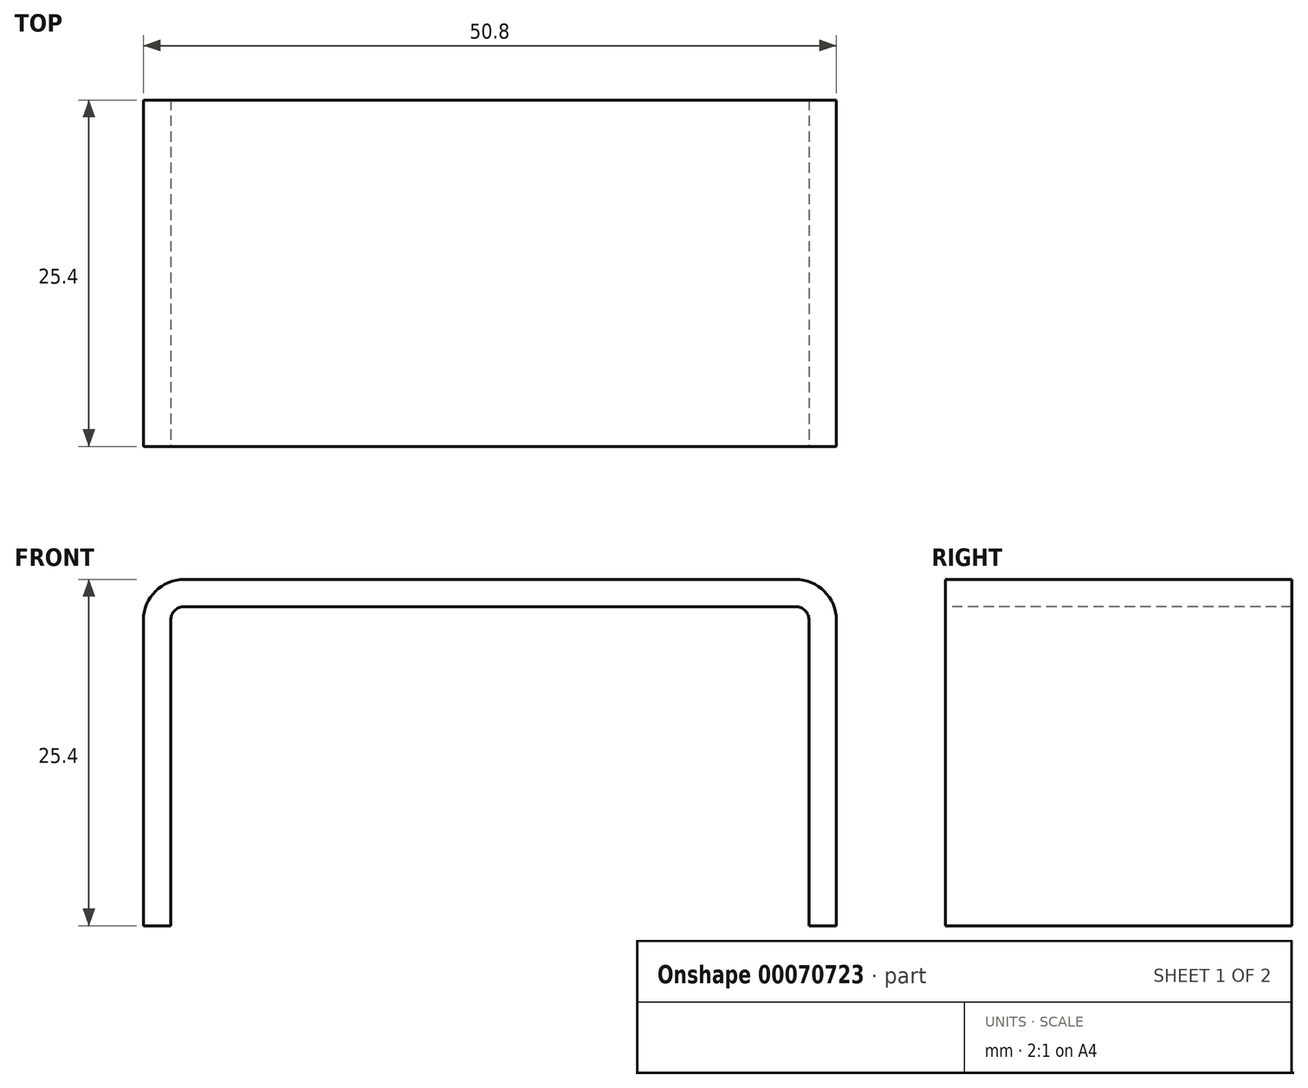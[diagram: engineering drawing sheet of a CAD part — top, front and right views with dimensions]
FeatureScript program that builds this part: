
annotation { "Feature Type Name" : "Feature", "Feature Type Description" : "" }
export const myFeature = defineFeature(function(context is Context, id is Id, definition is map)
    precondition{}
    {
        {
            var Q0;
            Q0=qCreatedBy(makeId("Front.planeOp"),FACE);
            var sketch = newSketch(context, id + "F0", { "sketchPlane" : qUnion([Q0])});
            skLineSegment(sketch, "E0.rect.bottom", {"start": v(25.4, -12.7) * mm, "end": v(-25.4, -12.7) * mm});
            skLineSegment(sketch, "E0.rect.top", {"start": v(25.4, 12.7) * mm, "end": v(-25.4, 12.7) * mm});
            skLineSegment(sketch, "E0.rect.left", {"start": v(25.4, -12.7) * mm, "end": v(25.4, 12.7) * mm});
            skLineSegment(sketch, "E0.rect.right", {"start": v(-25.4, -12.7) * mm, "end": v(-25.4, 12.7) * mm});
            skPoint(sketch, "E0.rect.middle", {"position": v(0, 0) * mm});
            skSolve(sketch);
        }
        {
            var Q0;
            Q0 = qSketchRegion(id + "F0", true);
            extrude(context, id + "F1", {"entities" : qUnion([Q0]), "depth" : 25.4 * mm, "symmetric" : true});
        }
        {
            var Q0;
            Q0=makeQuery(id+"F1.opExtrude","CAP_FACE",FACE,{"disambiguationData":[OSD([sQuery(id+"F0.wireOp",EDGE,"E0.rect.bottom"),sQuery(id+"F0.wireOp",EDGE,"E0.rect.top"),sQuery(id+"F0.wireOp",EDGE,"E0.rect.left"),sQuery(id+"F0.wireOp",EDGE,"E0.rect.right")])],"isStart":false});
            var sketch = newSketch(context, id + "F2", { "sketchPlane" : qUnion([Q0])});
            skLineSegment(sketch, "E1.bottom", {"start": v(-23.4, -12.7) * mm, "end": v(23.4, -12.7) * mm});
            skLineSegment(sketch, "E1.top", {"start": v(-23.4, 10.7) * mm, "end": v(23.4, 10.7) * mm});
            skLineSegment(sketch, "E1.left", {"start": v(-23.4, -12.7) * mm, "end": v(-23.4, 10.7) * mm});
            skLineSegment(sketch, "E1.right", {"start": v(23.4, -12.7) * mm, "end": v(23.4, 10.7) * mm});
            skSolve(sketch);
        }
        {
            var Q0;
            Q0 = qSketchRegion(id + "F2", true);
            var Q1;
            Q1=makeQuery(id+"F1.opExtrude","CAP_FACE",FACE,{"disambiguationData":[OSD([sQuery(id+"F0.wireOp",EDGE,"E0.rect.bottom"),sQuery(id+"F0.wireOp",EDGE,"E0.rect.top"),sQuery(id+"F0.wireOp",EDGE,"E0.rect.left"),sQuery(id+"F0.wireOp",EDGE,"E0.rect.right")])],"isStart":true});
            var Q2;
            Q2=makeQuery(id+"F1.opExtrude","SWEPT_BODY",BODY,{"disambiguationData":[OSD([sQuery(id+"F0.wireOp",EDGE,"E0.rect.bottom"),sQuery(id+"F0.wireOp",EDGE,"E0.rect.top"),sQuery(id+"F0.wireOp",EDGE,"E0.rect.left"),sQuery(id+"F0.wireOp",EDGE,"E0.rect.right")])]});
            extrude(context, id + "F3", {"entities" : qUnion([Q0]), "operationType" : NewBodyOperationType.REMOVE, "endBound" : BoundingType.UP_TO_NEXT, "oppositeDirection" : true, "endBoundEntityFace" : qUnion([Q1]), "endBoundEntityBody" : qUnion([Q2]), "depth" : 25 * mm});
        }
        {
            var Q0;
            Q0=makeQuery(id+"F1.opExtrude","SWEPT_EDGE",EDGE,{"disambiguationData":[OSD([sQuery(id+"F0.wireOp",EDGE,"E0.rect.top"),sQuery(id+"F0.wireOp",EDGE,"E0.rect.right")])]});
            var Q1;
            Q1=makeQuery(id+"F1.opExtrude","SWEPT_EDGE",EDGE,{"disambiguationData":[OSD([sQuery(id+"F0.wireOp",EDGE,"E0.rect.top"),sQuery(id+"F0.wireOp",EDGE,"E0.rect.left")])]});
            fillet(context, id + "F4", {"entities" : qUnion([Q0, Q1]), "radius" : 3 * mm, "tangentPropagation" : true, "allowEdgeOverflow" : false});
        }
        {
            var Q0;
            Q0=makeQuery(id+"F3.boolean.opBoolean","COPY",EDGE,{"derivedFrom":makeQuery(id+"F3.opExtrude","SWEPT_EDGE",EDGE,{"disambiguationData":[OSD([sQuery(id+"F2.wireOp",EDGE,"E1.top"),sQuery(id+"F2.wireOp",EDGE,"E1.left")])]})});
            var Q1;
            Q1=makeQuery(id+"F3.boolean.opBoolean","COPY",EDGE,{"derivedFrom":makeQuery(id+"F3.opExtrude","SWEPT_EDGE",EDGE,{"disambiguationData":[OSD([sQuery(id+"F2.wireOp",EDGE,"E1.top"),sQuery(id+"F2.wireOp",EDGE,"E1.right")])]})});
            fillet(context, id + "F5", {"entities" : qUnion([Q0, Q1]), "radius" : 1 * mm, "tangentPropagation" : true, "allowEdgeOverflow" : false});
        }
    });
